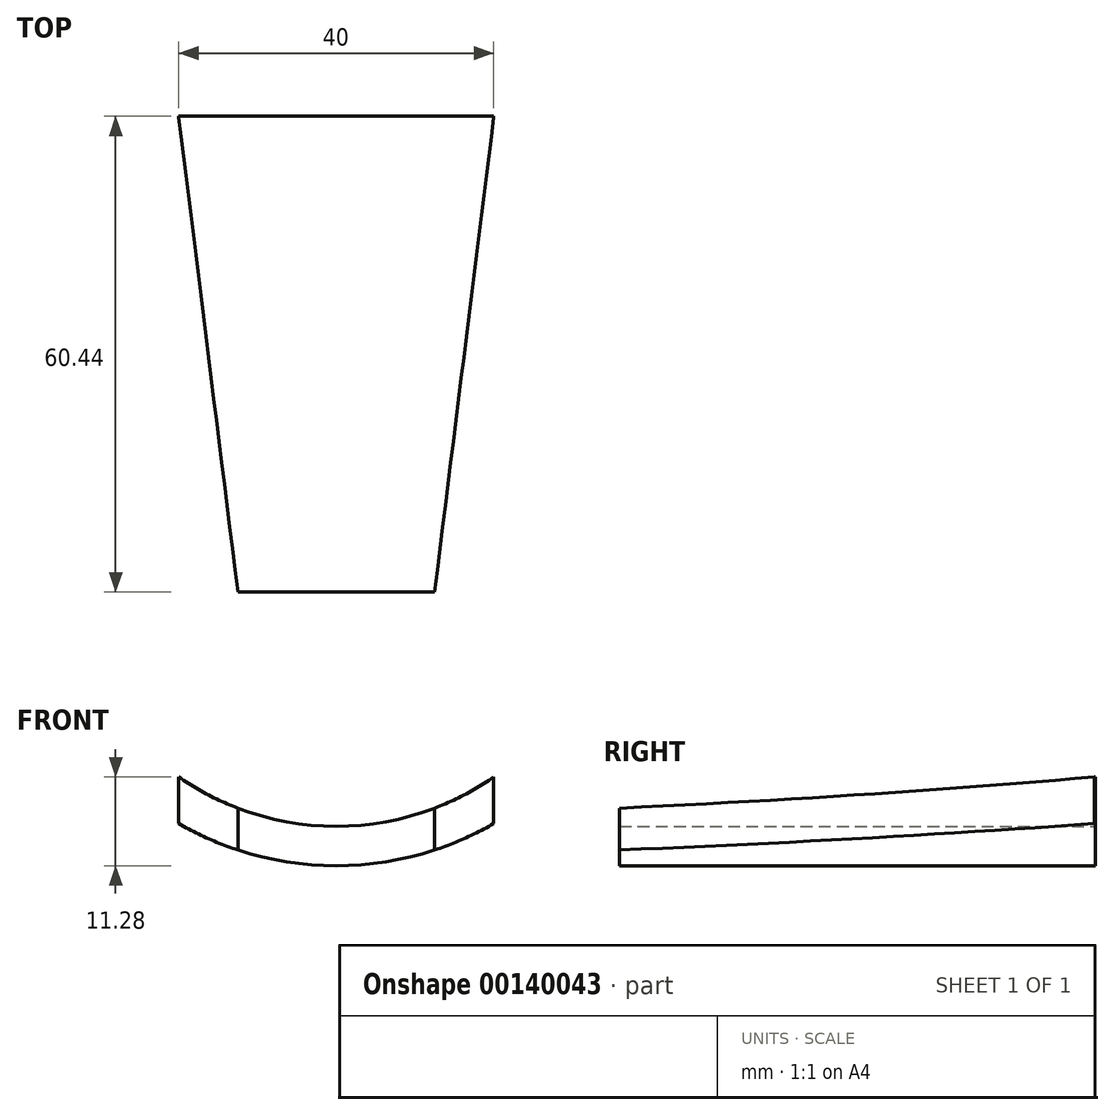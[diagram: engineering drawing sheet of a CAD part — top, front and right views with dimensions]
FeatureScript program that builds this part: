
annotation { "Feature Type Name" : "Feature", "Feature Type Description" : "" }
export const myFeature = defineFeature(function(context is Context, id is Id, definition is map)
    precondition{}
    {
        {
            var Q0;
            Q0=qCreatedBy(makeId("Top.planeOp"),FACE);
            var sketch = newSketch(context, id + "F0", { "sketchPlane" : qUnion([Q0])});
            skLineSegment(sketch, "E0", {"start": v(-12.5, 0) * mm, "end": v(12.5, 0) * mm});
            skLineSegment(sketch, "E1", {"start": v(12.5, 0) * mm, "end": v(20, 60.28) * mm});
            skLineSegment(sketch, "E2", {"start": v(-20, 60.28) * mm, "end": v(-12.5, 0) * mm});
            skLineSegment(sketch, "E3", {"start": v(-20, 60.28) * mm, "end": v(20, 60.28) * mm});
            skSolve(sketch);
        }
        {
            var Q0;
            Q0=qCreatedBy(makeId("Top.planeOp"),FACE);
            var sketch = newSketch(context, id + "F1", { "sketchPlane" : qUnion([Q0])});
            skLineSegment(sketch, "E4", {"start": v(0, 0) * mm, "end": v(0, 60.44) * mm});
            skSolve(sketch);
        }
        {
            var Q0;
            Q0=sQuery(id+"F0.wireOp",EDGE,"E3");
            cPlane(context, id + "F2", {"entities" : qUnion([Q0]), "cplaneType" : CPlaneType.LINE_ANGLE, "offset" : 25 * mm, "angle" : 0 * degree, "width" : 150 * mm, "height" : 150 * mm});
        }
        {
            var Q0;
            Q0=qCreatedBy(id+"F2.planeOp",FACE);
            var sketch = newSketch(context, id + "F3", { "sketchPlane" : qUnion([Q0])});
            skLineSegment(sketch, "E5", {"start": v(0, 0) * mm, "end": v(0, 5) * mm, "construction": true});
            skLineSegment(sketch, "E6", {"start": v(20, 5.36) * mm, "end": v(20, 11.28) * mm});
            skLineSegment(sketch, "E7.MirrorCS", {"start": v(-20, 5.36) * mm, "end": v(-20, 11.28) * mm});
            skArc(sketch, "E8", {"start": v(-20, 5.36) * mm, "mid": v(0, 0) * mm, "end": v(20, 5.36) * mm});
            skPoint(sketch, "E9.orphan", {"position": v(-20, 0) * mm});
            skPoint(sketch, "E10.start.orphan", {"position": v(20, 0) * mm});
            skArc(sketch, "E11.0", {"start": v(-20, 11.28) * mm, "mid": v(0, 5) * mm, "end": v(20, 11.28) * mm});
            skPoint(sketch, "E12.orphan", {"position": v(0, 0) * mm});
            skSolve(sketch);
        }
        {
            var Q0;
            Q0=sQuery(id+"F0.wireOp",EDGE,"E2");
            cPlane(context, id + "F4", {"entities" : qUnion([Q0]), "cplaneType" : CPlaneType.LINE_ANGLE, "offset" : 25 * mm, "angle" : 90 * degree, "width" : 150 * mm, "height" : 150 * mm});
        }
        {
            var Q0;
            Q0=sQuery(id+"F0.wireOp",EDGE,"E1");
            cPlane(context, id + "F5", {"entities" : qUnion([Q0]), "cplaneType" : CPlaneType.LINE_ANGLE, "offset" : 25 * mm, "angle" : 90 * degree, "width" : 150 * mm, "height" : 150 * mm});
        }
        {
            var Q0;
            Q0=makeQuery(id+"F3.imprint","IMPRINT",FACE,{"disambiguationData":[TD([[makeQuery(id+"F3.imprint","IMPRINT",EDGE,{"derivedFrom":sQuery(id+"F3.wireOp",EDGE,"E6")}),1.0]])]});
            var Q1;
            Q1=sQuery(id+"F1.wireOp",EDGE,"E4");
            sweep(context, id + "F6", {"profiles" : qUnion([Q0]), "path" : qUnion([Q1])});
        }
        {
            var Q0;
            Q0=makeQuery(id+"F6.opSweep","SWEPT_FACE",FACE,{"disambiguationData":[OSD([sQuery(id+"F1.wireOp",EDGE,"E4"),sQuery(id+"F3.wireOp",EDGE,"E6")])]});
            var Q1;
            Q1=qCreatedBy(id+"F4.planeOp",FACE);
            extrude(context, id + "F7", {"entities" : qUnion([Q0]), "operationType" : NewBodyOperationType.REMOVE, "endBound" : BoundingType.UP_TO_SURFACE, "oppositeDirection" : true, "endBoundEntityFace" : qUnion([Q1]), "depth" : 25 * mm, "hasDraft" : true, "draftAngle" : 30 * degree});
        }
        {
            var Q0;
            Q0=makeQuery(id+"F6.opSweep","SWEPT_FACE",FACE,{"disambiguationData":[OSD([sQuery(id+"F1.wireOp",EDGE,"E4"),sQuery(id+"F3.wireOp",EDGE,"E7.MirrorCS")])]});
            var Q1;
            Q1=qCreatedBy(id+"F5.planeOp",FACE);
            extrude(context, id + "F8", {"entities" : qUnion([Q0]), "operationType" : NewBodyOperationType.REMOVE, "endBound" : BoundingType.UP_TO_SURFACE, "oppositeDirection" : true, "endBoundEntityFace" : qUnion([Q1]), "depth" : 25 * mm, "hasDraft" : true, "draftAngle" : 30 * degree});
        }
    });
